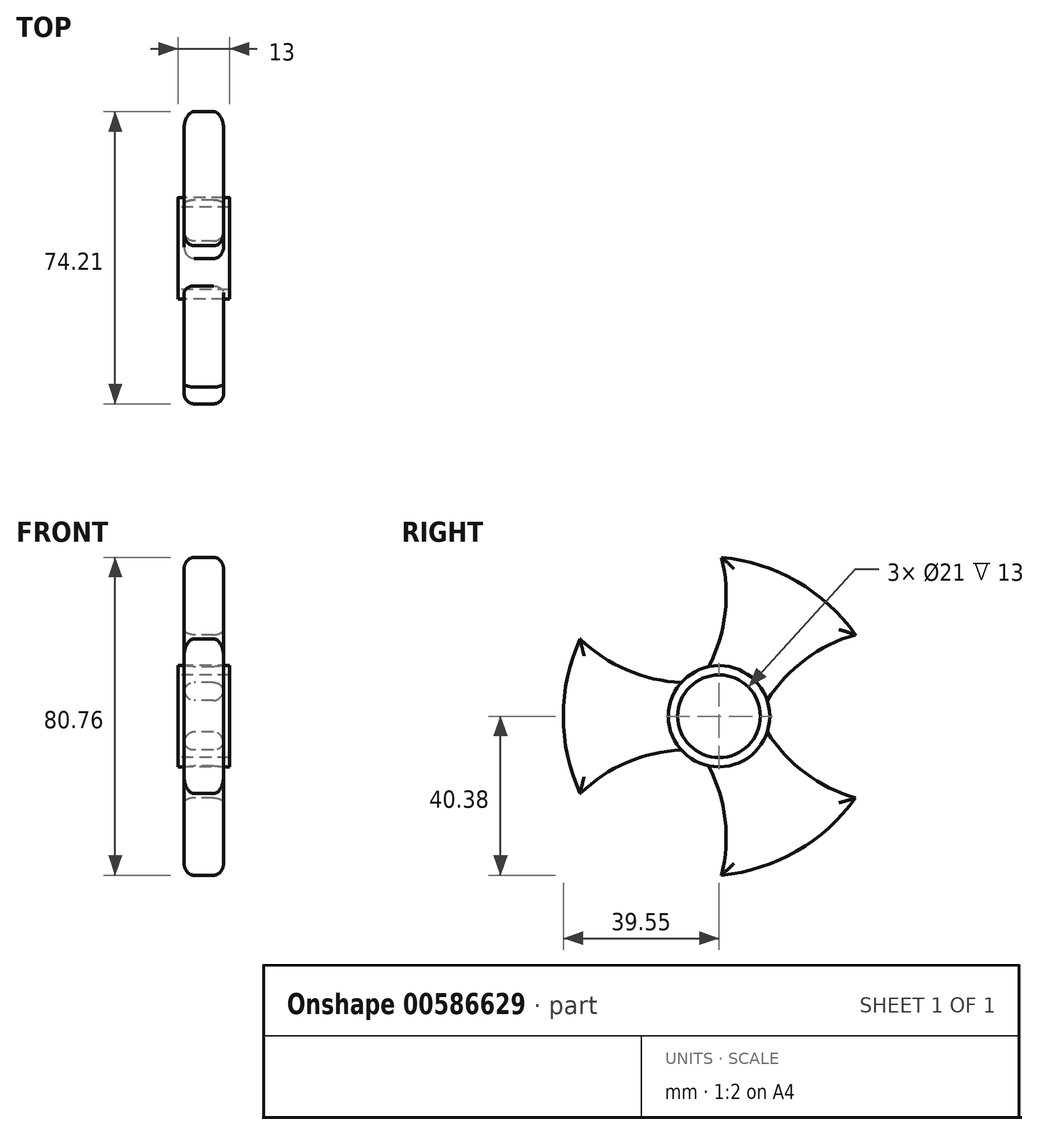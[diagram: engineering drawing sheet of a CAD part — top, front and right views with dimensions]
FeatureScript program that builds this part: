
annotation { "Feature Type Name" : "Feature", "Feature Type Description" : "" }
export const myFeature = defineFeature(function(context is Context, id is Id, definition is map)
    precondition{}
    {
        {
            var Q0;
            Q0=qCreatedBy(makeId("Right.planeOp"),FACE);
            var sketch = newSketch(context, id + "F0", { "sketchPlane" : qUnion([Q0])});
            skCircle(sketch, "E0", {"center": v(0, 0) * mm, "radius": 10.5 * mm});
            skCircle(sketch, "E1", {"center": v(0, 0) * mm, "radius": 12.87 * mm});
            skArc(sketch, "E2", {"start": v(-35.27, 19.66) * mm, "mid": v(-39.55, 0) * mm, "end": v(-35.27, -19.66) * mm});
            skArc(sketch, "E3", {"start": v(-9.58, -8.6) * mm, "mid": v(-23.45, -11.75) * mm, "end": v(-35.27, -19.66) * mm});
            skArc(sketch, "E4", {"start": v(-35.27, 19.66) * mm, "mid": v(-23.45, 11.75) * mm, "end": v(-9.58, 8.6) * mm});
            skSolve(sketch);
        }
        {
            var Q0;
            Q0=makeQuery(id+"F0.imprint","IMPRINT",FACE,{"disambiguationData":[TD([[makeQuery(id+"F0.imprint","IMPRINT",EDGE,{"derivedFrom":sQuery(id+"F0.wireOp",EDGE,"E0")}),-1.0]])]});
            extrude(context, id + "F1", {"entities" : qUnion([Q0]), "depth" : 6.5 * mm, "offsetDistance" : 25.4 * mm, "hasSecondDirection" : true, "secondDirectionOppositeDirection" : true, "secondDirectionDepth" : 6.5 * mm});
        }
        {
            var Q0;
            Q0=makeQuery(id+"F0.imprint","IMPRINT",FACE,{"disambiguationData":[TD([[makeQuery(id+"F0.imprint","IMPRINT",EDGE,{"derivedFrom":sQuery(id+"F0.wireOp",EDGE,"E2")}),1.0]])]});
            extrude(context, id + "F2", {"entities" : qUnion([Q0]), "operationType" : NewBodyOperationType.ADD, "depth" : 5 * mm, "offsetDistance" : 25.4 * mm, "hasSecondDirection" : true, "secondDirectionOppositeDirection" : true, "secondDirectionDepth" : 5 * mm});
        }
        {
            var Q0;
            Q0=makeQuery(id+"F2.opExtrude","CAP_EDGE",EDGE,{"disambiguationData":[OSD([sQuery(id+"F0.wireOp",EDGE,"E4")])],"isStart":false});
            var Q1;
            Q1=makeQuery(id+"F2.opExtrude","CAP_EDGE",EDGE,{"disambiguationData":[OSD([sQuery(id+"F0.wireOp",EDGE,"E3")])],"isStart":false});
            var Q2;
            Q2=makeQuery(id+"F2.opExtrude","CAP_EDGE",EDGE,{"disambiguationData":[OSD([sQuery(id+"F0.wireOp",EDGE,"E2")])],"isStart":false});
            var Q3;
            Q3=makeQuery(id+"F2.opExtrude","CAP_EDGE",EDGE,{"disambiguationData":[OSD([sQuery(id+"F0.wireOp",EDGE,"E4")])],"isStart":true});
            var Q4;
            Q4=makeQuery(id+"F2.opExtrude","CAP_EDGE",EDGE,{"disambiguationData":[OSD([sQuery(id+"F0.wireOp",EDGE,"E2")])],"isStart":true});
            var Q5;
            Q5=makeQuery(id+"F2.opExtrude","CAP_EDGE",EDGE,{"disambiguationData":[OSD([sQuery(id+"F0.wireOp",EDGE,"E3")])],"isStart":true});
            fillet(context, id + "F3", {"entities" : qUnion([Q0, Q1, Q2, Q3, Q4, Q5]), "radius" : 2.54 * mm, "tangentPropagation" : true, "allowEdgeOverflow" : false});
        }
        {
            var Q0;
            Q0=makeQuery(id+"F1.opExtrude","SWEPT_BODY",BODY,{"disambiguationData":[OSD([sQuery(id+"F0.wireOp",EDGE,"E0"),sQuery(id+"F0.wireOp",EDGE,"E1")])]});
            var Q1;
            Q1=makeQuery(id+"F1.opExtrude","CAP_EDGE",EDGE,{"disambiguationData":[OSD([sQuery(id+"F0.wireOp",EDGE,"E1")])],"isStart":false});
            circularPattern(context, id + "F4", {"entities" : qUnion([Q0]), "axis" : qUnion([Q1]), "angle" : 360 * degree, "instanceCount" : 3, "equalSpace" : true});
        }
    });
